# Revit family: R586SEFL
name_source: partatom
category: Pipe Accessories
units: mm (PartAtom-declared; Revit-internal decimal feet)

## family parameters
Always vertical = No
Cut with Voids When Loaded = No
Part Type = Normal
Round Connector Dimension = Use Diameter
Shared = No
Work Plane-Based = No

## types (2) — shared parameters
D1 = 66 mm  [stored 0.216535 ft]
D2 = 60 mm  [stored 0.19685 ft]
Description = Collector for heating plant with hydraulic separator, flanged and threaded connections
GIA_Fluid for use = Water , glycol solution (max. 50% glycol)
GIA_Maximum Operating Pressure = 6 bar
GIA_Temperature range = 5÷110 °C
I1 = 160 mm  [stored 0.524934 ft]
I2 = 174 mm  [stored 0.570866 ft]
L2 = 360 mm  [stored 1.1811 ft]
Manufacturer = Giacomini
Primary Nominal Diameter = 65 mm  [stored 0.213255 ft]
R1 = 33 mm  [stored 0.108268 ft]
Secondary Nominal Diameter = 40 mm  [stored 0.131234 ft]
URL = giacomini.com
zero-valued in all types: Default Elevation

## per-type parameters (varying)
| type | C1 | Code | L1 | L3 | L4 | L5 | Legth | Secondary Outlet Array Value | Width |
| 2 Derivations | No | R586SEY22 | 265 mm | 120 mm  [stored 0.393701 ft] | 180 mm | 628 mm | 789 mm | 2 | 100 mm  [stored 0.328084 ft] |
| 3 Derivations | Yes | R586SEY23 | 343 mm | 183 mm | 231 mm | 668 mm  [stored 2.1916 ft] | 1093 mm  [stored 3.58596 ft] | 3 | 150 mm |

note: column(s) folded — value = type name in every type: Model

note: [stored X ft] marks values corroborated as IEEE doubles in the binary element streams (Revit-internal decimal feet)

## geometry (parser evidence)
native form markers: Sweep x14
no freeform markers — native parametric forms only
